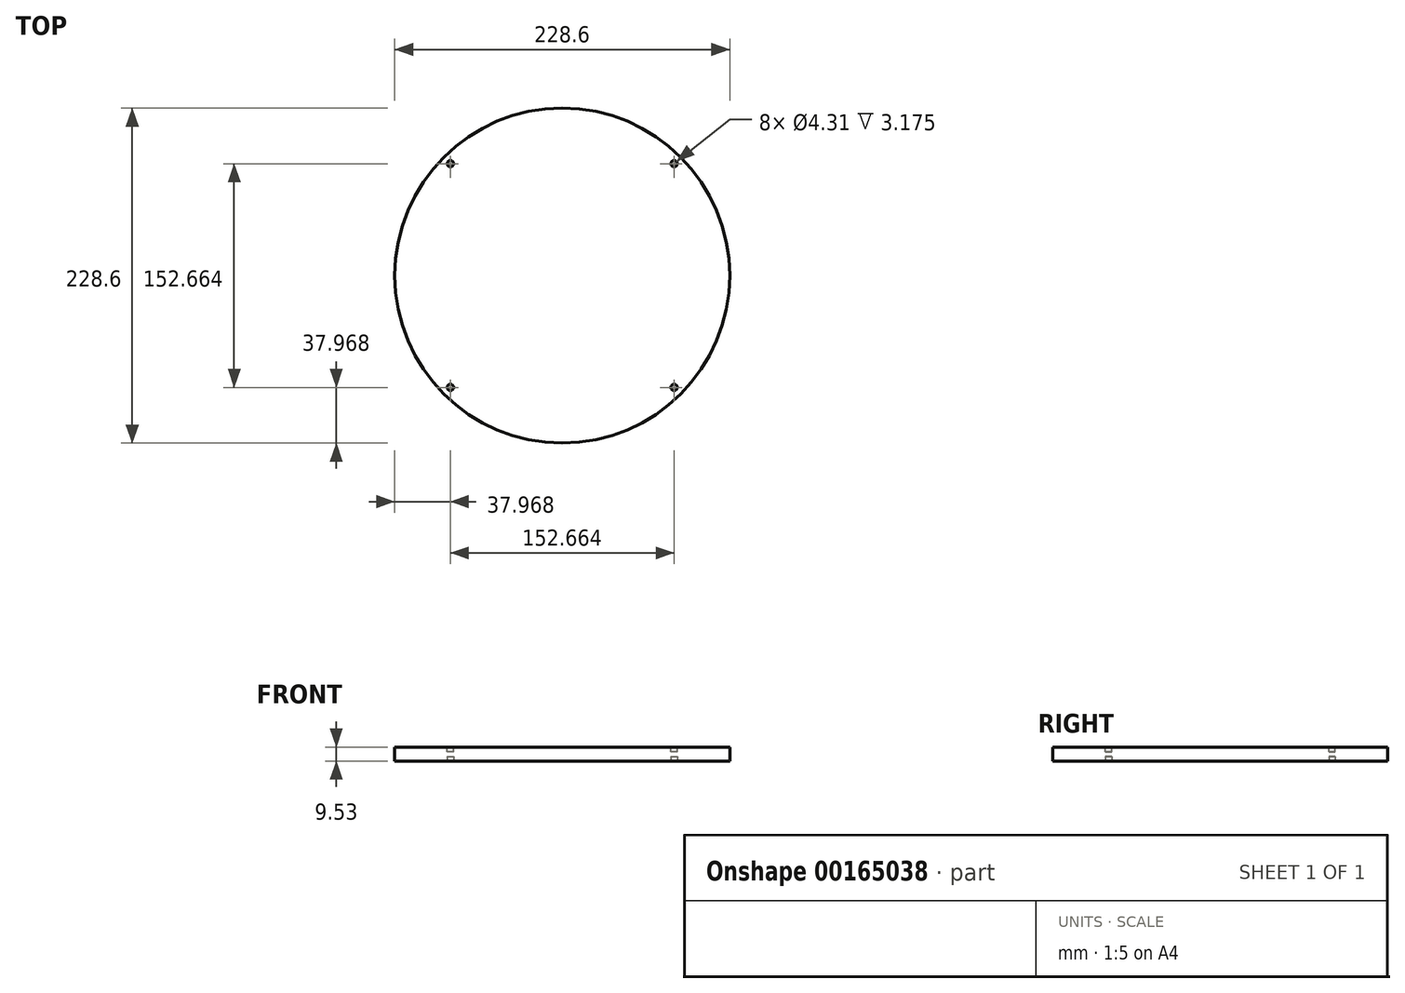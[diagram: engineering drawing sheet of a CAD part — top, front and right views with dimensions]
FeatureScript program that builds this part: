
annotation { "Feature Type Name" : "Feature", "Feature Type Description" : "" }
export const myFeature = defineFeature(function(context is Context, id is Id, definition is map)
    precondition{}
    {
        {
            var Q0;
            Q0=qCreatedBy(makeId("Top.planeOp"),FACE);
            var sketch = newSketch(context, id + "F0", { "sketchPlane" : qUnion([Q0])});
            skCircle(sketch, "E0", {"center": v(0, 0) * mm, "radius": 114.3 * mm});
            skSolve(sketch);
        }
        {
            var Q0;
            Q0 = qSketchRegion(id + "F0", true);
            extrude(context, id + "F1", {"entities" : qUnion([Q0]), "depth" : 9.52 * mm});
        }
        {
            var Q0;
            Q0=makeQuery(id+"F1.opExtrude","CAP_FACE",FACE,{"disambiguationData":[OSD([sQuery(id+"F0.wireOp",EDGE,"E0")])],"isStart":false});
            var sketch = newSketch(context, id + "F2", { "sketchPlane" : qUnion([Q0])});
            skLineSegment(sketch, "E1.bottom", {"start": v(76.33, 76.33) * mm, "end": v(-76.33, 76.33) * mm, "construction": true});
            skLineSegment(sketch, "E1.top", {"start": v(76.33, -76.33) * mm, "end": v(-76.33, -76.33) * mm, "construction": true});
            skLineSegment(sketch, "E1.left", {"start": v(76.33, 76.33) * mm, "end": v(76.33, -76.33) * mm, "construction": true});
            skLineSegment(sketch, "E1.right", {"start": v(-76.33, 76.33) * mm, "end": v(-76.33, -76.33) * mm, "construction": true});
            skPoint(sketch, "E1.middle", {"position": v(0, 0) * mm});
            skCircle(sketch, "E2", {"center": v(76.33, 76.33) * mm, "radius": 6.35 * mm, "construction": true});
            skCircle(sketch, "E3", {"center": v(-76.33, 76.33) * mm, "radius": 2.15 * mm});
            skCircle(sketch, "E4", {"center": v(76.33, 76.33) * mm, "radius": 2.15 * mm});
            skCircle(sketch, "E5", {"center": v(76.33, -76.33) * mm, "radius": 2.15 * mm});
            skCircle(sketch, "E6", {"center": v(-76.33, -76.33) * mm, "radius": 2.15 * mm});
            skSolve(sketch);
        }
        {
            var Q0;
            Q0 = qSketchRegion(id + "F2", true);
            extrude(context, id + "F3", {"entities" : qUnion([Q0]), "operationType" : NewBodyOperationType.REMOVE, "oppositeDirection" : true, "depth" : 3.17 * mm});
        }
        {
            var Q0;
            Q0=makeQuery(id+"F1.opExtrude","CAP_FACE",FACE,{"disambiguationData":[OSD([sQuery(id+"F0.wireOp",EDGE,"E0")])],"isStart":true});
            var sketch = newSketch(context, id + "F4", { "sketchPlane" : qUnion([Q0])});
            skCircle(sketch, "E7", {"center": v(-76.33, 76.33) * mm, "radius": 2.15 * mm});
            skCircle(sketch, "E8", {"center": v(76.33, 76.33) * mm, "radius": 2.15 * mm});
            skCircle(sketch, "E9", {"center": v(76.33, -76.33) * mm, "radius": 2.15 * mm});
            skCircle(sketch, "E10", {"center": v(-76.33, -76.33) * mm, "radius": 2.15 * mm});
            skSolve(sketch);
        }
        {
            var Q0;
            Q0 = qSketchRegion(id + "F4", true);
            extrude(context, id + "F5", {"entities" : qUnion([Q0]), "operationType" : NewBodyOperationType.REMOVE, "oppositeDirection" : true, "depth" : 3.17 * mm});
        }
    });
